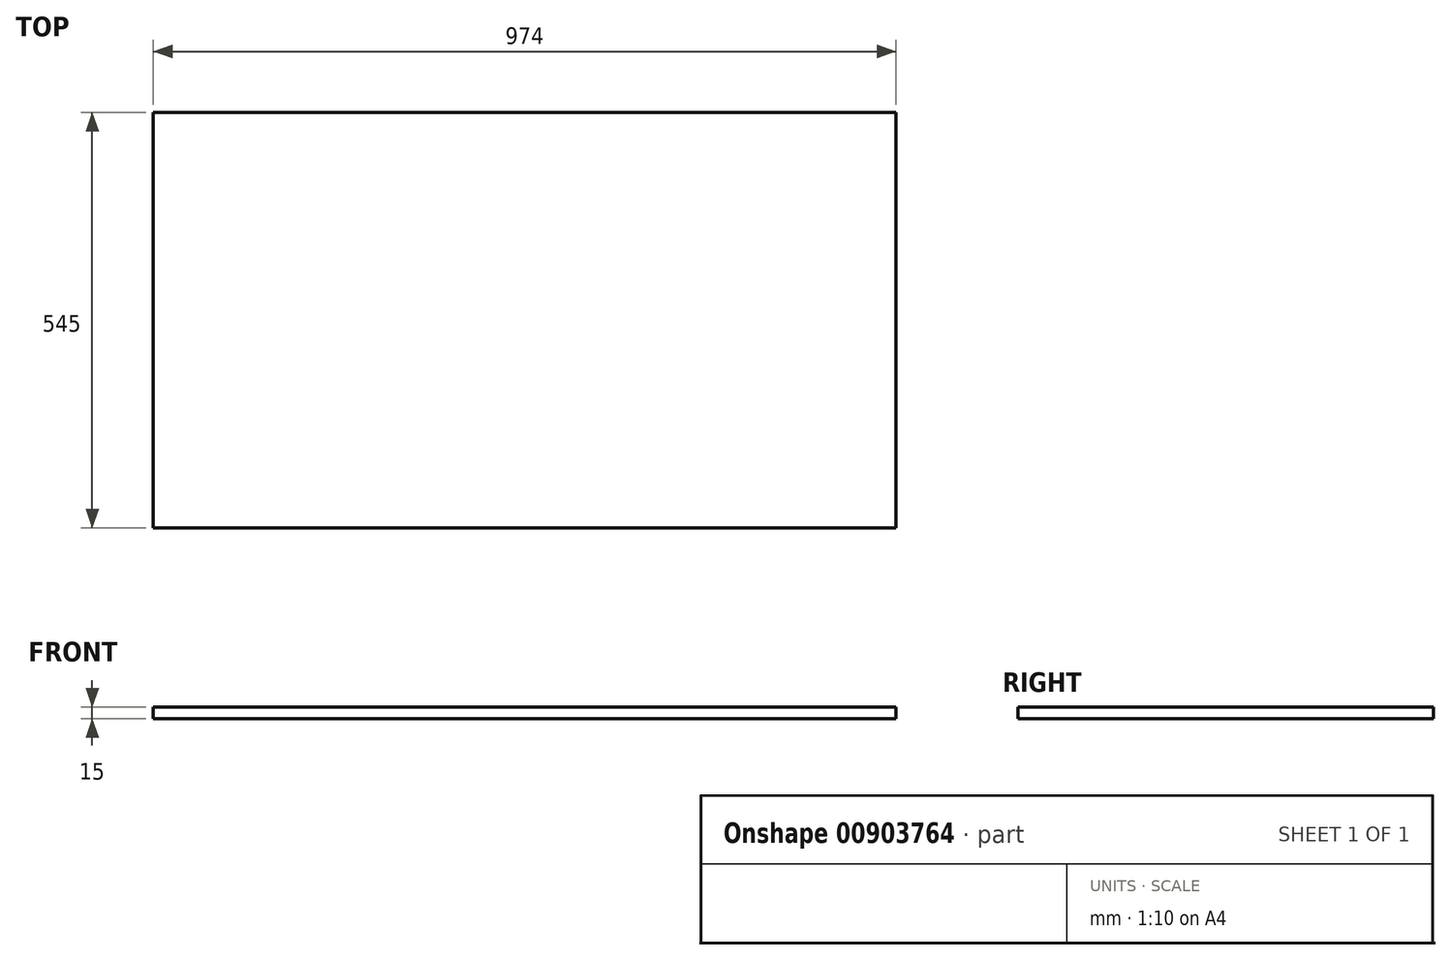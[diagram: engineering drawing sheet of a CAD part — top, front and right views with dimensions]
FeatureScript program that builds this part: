
annotation { "Feature Type Name" : "Feature", "Feature Type Description" : "" }
export const myFeature = defineFeature(function(context is Context, id is Id, definition is map)
    precondition{}
    {
        {
            var Q0;
            Q0=qCreatedBy(makeId("Top.planeOp"),FACE);
            var sketch = newSketch(context, id + "F0", { "sketchPlane" : qUnion([Q0])});
            skLineSegment(sketch, "E0.bottom", {"start": v(-487, 272.5) * mm, "end": v(487, 272.5) * mm});
            skLineSegment(sketch, "E0.top", {"start": v(-487, -272.5) * mm, "end": v(487, -272.5) * mm});
            skLineSegment(sketch, "E0.left", {"start": v(-487, 272.5) * mm, "end": v(-487, -272.5) * mm});
            skLineSegment(sketch, "E0.right", {"start": v(487, 272.5) * mm, "end": v(487, -272.5) * mm});
            skSolve(sketch);
        }
        {
            var Q0;
            Q0=makeQuery(id+"F0.imprint","IMPRINT",FACE,{"disambiguationData":[TD([[makeQuery(id+"F0.imprint","IMPRINT",EDGE,{"derivedFrom":sQuery(id+"F0.wireOp",EDGE,"E0.bottom")}),-1.0]])]});
            extrude(context, id + "F1", {"entities" : qUnion([Q0]), "depth" : 15 * mm, "offsetDistance" : 25 * mm});
        }
    });
